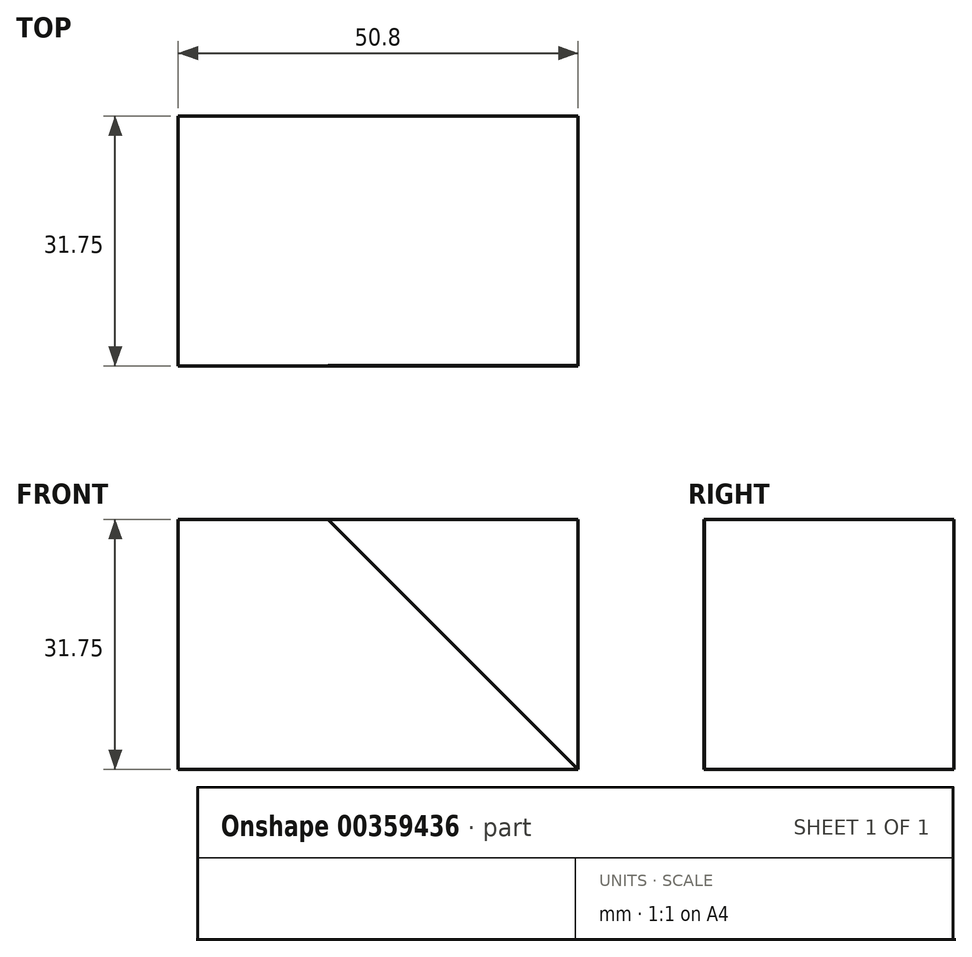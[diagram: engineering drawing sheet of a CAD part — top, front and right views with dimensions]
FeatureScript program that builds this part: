
annotation { "Feature Type Name" : "Feature", "Feature Type Description" : "" }
export const myFeature = defineFeature(function(context is Context, id is Id, definition is map)
    precondition{}
    {
        {
            var Q0;
            Q0=qCreatedBy(makeId("Front.planeOp"),FACE);
            var sketch = newSketch(context, id + "F0", { "sketchPlane" : qUnion([Q0])});
            skLineSegment(sketch, "E0", {"start": v(0, 0) * mm, "end": v(0, 31.75) * mm});
            skLineSegment(sketch, "E1", {"start": v(0, 31.75) * mm, "end": v(50.8, 31.75) * mm});
            skLineSegment(sketch, "E2", {"start": v(50.8, 31.75) * mm, "end": v(50.8, 0) * mm});
            skLineSegment(sketch, "E3", {"start": v(50.8, 0) * mm, "end": v(0, 0) * mm});
            skSolve(sketch);
        }
        {
            var Q0;
            Q0=makeQuery(id+"F0.imprint","IMPRINT",FACE,{"disambiguationData":[TD([[makeQuery(id+"F0.imprint","IMPRINT",EDGE,{"derivedFrom":sQuery(id+"F0.wireOp",EDGE,"E0")}),-1.0]])]});
            extrude(context, id + "F1", {"entities" : qUnion([Q0]), "depth" : 31.75 * mm});
        }
        {
            var Q0;
            Q0=makeQuery(id+"F1.opExtrude","CAP_FACE",FACE,{"disambiguationData":[OSD([sQuery(id+"F0.wireOp",EDGE,"E0"),sQuery(id+"F0.wireOp",EDGE,"E1"),sQuery(id+"F0.wireOp",EDGE,"E2"),sQuery(id+"F0.wireOp",EDGE,"E3")])],"isStart":false});
            var sketch = newSketch(context, id + "F2", { "sketchPlane" : qUnion([Q0])});
            skLineSegment(sketch, "E4", {"start": v(50.8, 0) * mm, "end": v(50.8, 31.75) * mm});
            skLineSegment(sketch, "E5", {"start": v(50.8, 31.75) * mm, "end": v(19.05, 31.75) * mm});
            skLineSegment(sketch, "E6", {"start": v(19.05, 31.75) * mm, "end": v(50.8, 0) * mm});
            skSolve(sketch);
        }
        {
            var Q0;
            Q0=makeQuery(id+"F2.imprint","IMPRINT",FACE,{"disambiguationData":[TD([[makeQuery(id+"F2.imprint","IMPRINT",EDGE,{"derivedFrom":sQuery(id+"F2.wireOp",EDGE,"E4")}),-1.0]])]});
            extrude(context, id + "F3", {"entities" : qUnion([Q0]), "operationType" : NewBodyOperationType.REMOVE, "oppositeDirection" : true, "depth" : 5 / 101.6 * mm});
        }
        {
            var Q0;
            Q0=makeQuery(id+"F1.opExtrude","CAP_FACE",FACE,{"disambiguationData":[OSD([sQuery(id+"F0.wireOp",EDGE,"E0"),sQuery(id+"F0.wireOp",EDGE,"E1"),sQuery(id+"F0.wireOp",EDGE,"E2"),sQuery(id+"F0.wireOp",EDGE,"E3")])],"isStart":true});
            var sketch = newSketch(context, id + "F4", { "sketchPlane" : qUnion([Q0])});
            skLineSegment(sketch, "E7", {"start": v(-50.8, 0) * mm, "end": v(-50.8, 19.65) * mm});
            skLineSegment(sketch, "E8", {"start": v(-50.8, 19.65) * mm, "end": v(-31.15, 19.65) * mm});
            skLineSegment(sketch, "E9", {"start": v(-31.15, 19.65) * mm, "end": v(-50.8, 0) * mm});
            skSolve(sketch);
        }
        {
            var Q0;
            Q0 = qSketchRegion(id + "F4", true);
            extrude(context, id + "F5", {"entities" : qUnion([Q0]), "operationType" : NewBodyOperationType.ADD, "oppositeDirection" : true, "depth" : 19.05 * mm});
        }
    });
